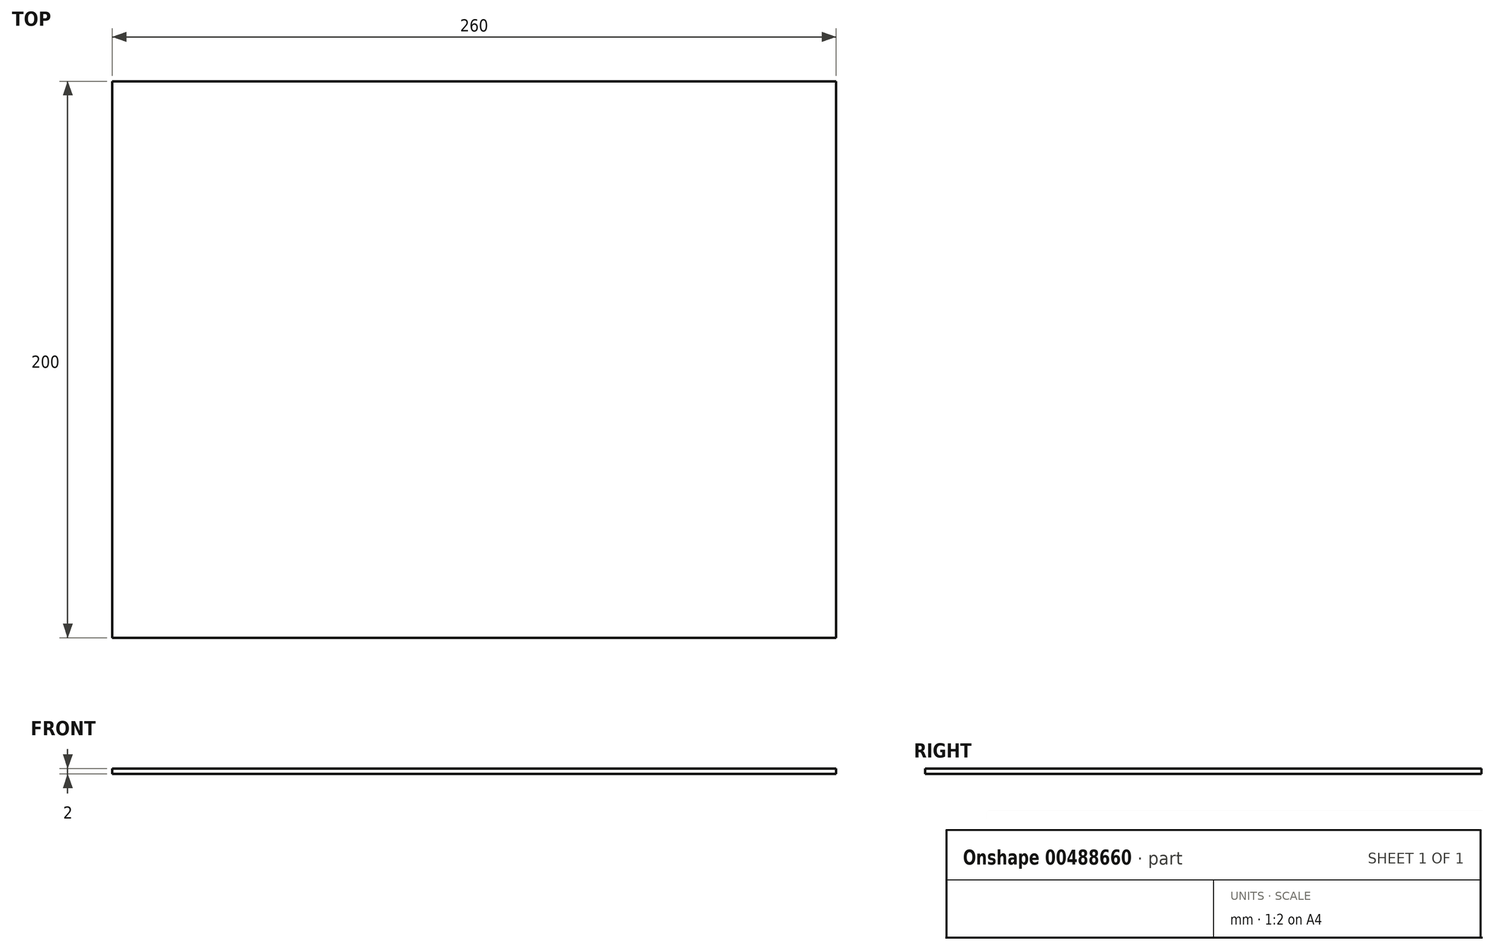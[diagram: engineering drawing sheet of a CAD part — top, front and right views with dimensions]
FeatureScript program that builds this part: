
annotation { "Feature Type Name" : "Feature", "Feature Type Description" : "" }
export const myFeature = defineFeature(function(context is Context, id is Id, definition is map)
    precondition{}
    {
        {
            var Q0;
            Q0=qCreatedBy(makeId("Top.planeOp"),FACE);
            var sketch = newSketch(context, id + "F0", { "sketchPlane" : qUnion([Q0])});
            skLineSegment(sketch, "E0.bottom", {"start": v(-130, 0) * mm, "end": v(130, 0) * mm});
            skLineSegment(sketch, "E0.top", {"start": v(-130, -200) * mm, "end": v(130, -200) * mm});
            skLineSegment(sketch, "E0.left", {"start": v(-130, 0) * mm, "end": v(-130, -200) * mm});
            skLineSegment(sketch, "E0.right", {"start": v(130, 0) * mm, "end": v(130, -200) * mm});
            skSolve(sketch);
        }
        {
            var Q0;
            Q0 = qSketchRegion(id + "F0", true);
            extrude(context, id + "F1", {"entities" : qUnion([Q0]), "depth" : 2 * mm});
        }
    });
